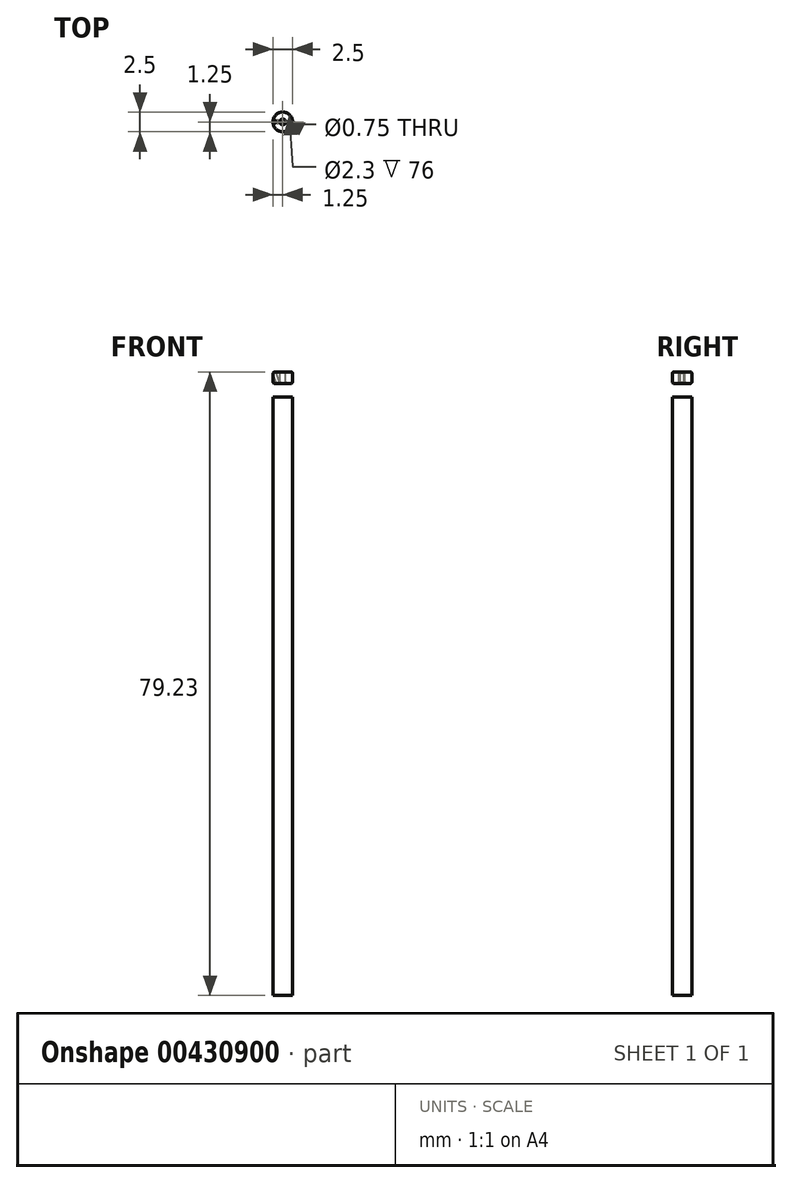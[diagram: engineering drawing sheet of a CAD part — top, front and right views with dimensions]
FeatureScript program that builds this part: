
annotation { "Feature Type Name" : "Feature", "Feature Type Description" : "" }
export const myFeature = defineFeature(function(context is Context, id is Id, definition is map)
    precondition{}
    {
        {
            var Q0;
            Q0=qCreatedBy(makeId("Front.planeOp"),FACE);
            var sketch = newSketch(context, id + "F0", { "sketchPlane" : qUnion([Q0])});
            skLineSegment(sketch, "E0", {"start": v(0, 64.55) * mm, "end": v(0, -76.58) * mm, "construction": true});
            skLineSegment(sketch, "E1.bottom", {"start": v(1.15, 0) * mm, "end": v(1.25, 0) * mm});
            skLineSegment(sketch, "E1.top", {"start": v(1.15, -76) * mm, "end": v(1.25, -76) * mm});
            skLineSegment(sketch, "E1.left", {"start": v(1.15, 0) * mm, "end": v(1.15, -76) * mm});
            skLineSegment(sketch, "E1.right", {"start": v(1.25, 0) * mm, "end": v(1.25, -76) * mm});
            skSolve(sketch);
        }
        {
            var Q0;
            Q0=makeQuery(id+"F0.imprint","IMPRINT",FACE,{"disambiguationData":[TD([[makeQuery(id+"F0.imprint","IMPRINT",EDGE,{"derivedFrom":sQuery(id+"F0.wireOp",EDGE,"E1.bottom")}),-1.0]])]});
            var Q1;
            Q1=sQuery(id+"F0.wireOp",EDGE,"E0");
            revolve(context, id + "F1", {"entities" : qUnion([Q0]), "axis" : qUnion([Q1]), "revolveType" : RevolveType.FULL});
        }
        {
            var Q0;
            Q0=qCreatedBy(makeId("Front.planeOp"),FACE);
            var sketch = newSketch(context, id + "F2", { "sketchPlane" : qUnion([Q0])});
            skLineSegment(sketch, "E2", {"start": v(0, 6.15) * mm, "end": v(0, -0.92) * mm, "construction": true});
            skLineSegment(sketch, "E3.bottom", {"start": v(0, 1.73) * mm, "end": v(-1.25, 1.73) * mm});
            skLineSegment(sketch, "E3.top", {"start": v(0, 3.23) * mm, "end": v(-1.25, 3.23) * mm});
            skLineSegment(sketch, "E3.left", {"start": v(0, 1.73) * mm, "end": v(0, 3.23) * mm});
            skLineSegment(sketch, "E3.right", {"start": v(-1.25, 1.73) * mm, "end": v(-1.25, 3.23) * mm});
            skLineSegment(sketch, "E4", {"start": v(-0.37, 3.23) * mm, "end": v(-0.37, 1.73) * mm});
            skSolve(sketch);
        }
        {
            var Q0;
            {var subQ0=sQuery(id+"F2.wireOp",EDGE,"E3.right");Q0=makeQuery(id+"F2.imprint","IMPRINT",FACE,{"disambiguationData":[TD([[makeQuery(id+"F2.imprint","IMPRINT",EDGE,{"derivedFrom":subQ0}),-1.0]])]});}
            var Q1;
            Q1=sQuery(id+"F2.wireOp",EDGE,"E2");
            revolve(context, id + "F3", {"entities" : qUnion([Q0]), "axis" : qUnion([Q1]), "revolveType" : RevolveType.FULL});
        }
        {
            var Q0;
            Q0=qCreatedBy(makeId("Front.planeOp"),FACE);
            var sketch = newSketch(context, id + "F4", { "sketchPlane" : qUnion([Q0])});
            skLineSegment(sketch, "E5", {"start": v(-1.1, 3.23) * mm, "end": v(-0.55, 1.73) * mm});
            skLineSegment(sketch, "E6.0", {"start": v(-1.25, 3.23) * mm, "end": v(1.25, 3.23) * mm, "construction": true});
            skLineSegment(sketch, "E7.0", {"start": v(-1.25, 1.73) * mm, "end": v(1.25, 1.73) * mm, "construction": true});
            skSolve(sketch);
        }
        {
            var Q0;
            Q0=qCreatedBy(makeId("Front.planeOp"),FACE);
            var sketch = newSketch(context, id + "F5", { "sketchPlane" : qUnion([Q0])});
            skLineSegment(sketch, "E8.0", {"start": v(-1.1, 3.23) * mm, "end": v(-0.55, 1.73) * mm, "construction": true});
            skLineSegment(sketch, "E9", {"start": v(-1.04, 3.68) * mm, "end": v(-0.16, 1.28) * mm});
            skLineSegment(sketch, "E10", {"start": v(-0.16, 1.28) * mm, "end": v(-0.36, 1.2) * mm});
            skLineSegment(sketch, "E11", {"start": v(-1.04, 3.68) * mm, "end": v(-1.24, 3.6) * mm});
            skLineSegment(sketch, "E12", {"start": v(-1.24, 3.6) * mm, "end": v(-0.36, 1.2) * mm});
            skSolve(sketch);
        }
        {
            var Q0;
            Q0=makeQuery(id+"F5.imprint","IMPRINT",FACE,{"disambiguationData":[TD([[makeQuery(id+"F5.imprint","IMPRINT",EDGE,{"derivedFrom":sQuery(id+"F5.wireOp",EDGE,"E9")}),-1.0]])]});
            var Q1;
            Q1=sQuery(id+"F5.wireOp",EDGE,"E12");
            revolve(context, id + "F6", {"operationType" : NewBodyOperationType.REMOVE, "entities" : qUnion([Q0]), "axis" : qUnion([Q1]), "revolveType" : RevolveType.FULL});
        }
        {
            var Q0;
            Q0=makeQuery(id+"F3.opRevolve","SWEPT_EDGE",EDGE,{"disambiguationData":[OSD([sQuery(id+"F2.wireOp",EDGE,"E3.top"),sQuery(id+"F2.wireOp",EDGE,"E4")])]});
            var Q1;
            Q1=makeQuery(id+"F3.opRevolve","SWEPT_EDGE",EDGE,{"disambiguationData":[OSD([sQuery(id+"F2.wireOp",EDGE,"E3.bottom"),sQuery(id+"F2.wireOp",EDGE,"E4")])]});
            fillet(context, id + "F7", {"entities" : qUnion([Q0, Q1]), "radius" : .25 * mm, "tangentPropagation" : true, "allowEdgeOverflow" : false});
        }
        {
            var Q0;
            Q0=makeQuery(id+"F3.opRevolve","SWEPT_EDGE",EDGE,{"disambiguationData":[OSD([sQuery(id+"F2.wireOp",EDGE,"E3.top"),sQuery(id+"F2.wireOp",EDGE,"E3.right")])]});
            var Q1;
            Q1=makeQuery(id+"F3.opRevolve","SWEPT_EDGE",EDGE,{"disambiguationData":[OSD([sQuery(id+"F2.wireOp",EDGE,"E3.bottom"),sQuery(id+"F2.wireOp",EDGE,"E3.right")])]});
            fillet(context, id + "F8", {"entities" : qUnion([Q0, Q1]), "radius" : .25 * mm, "tangentPropagation" : true, "allowEdgeOverflow" : false});
        }
    });
